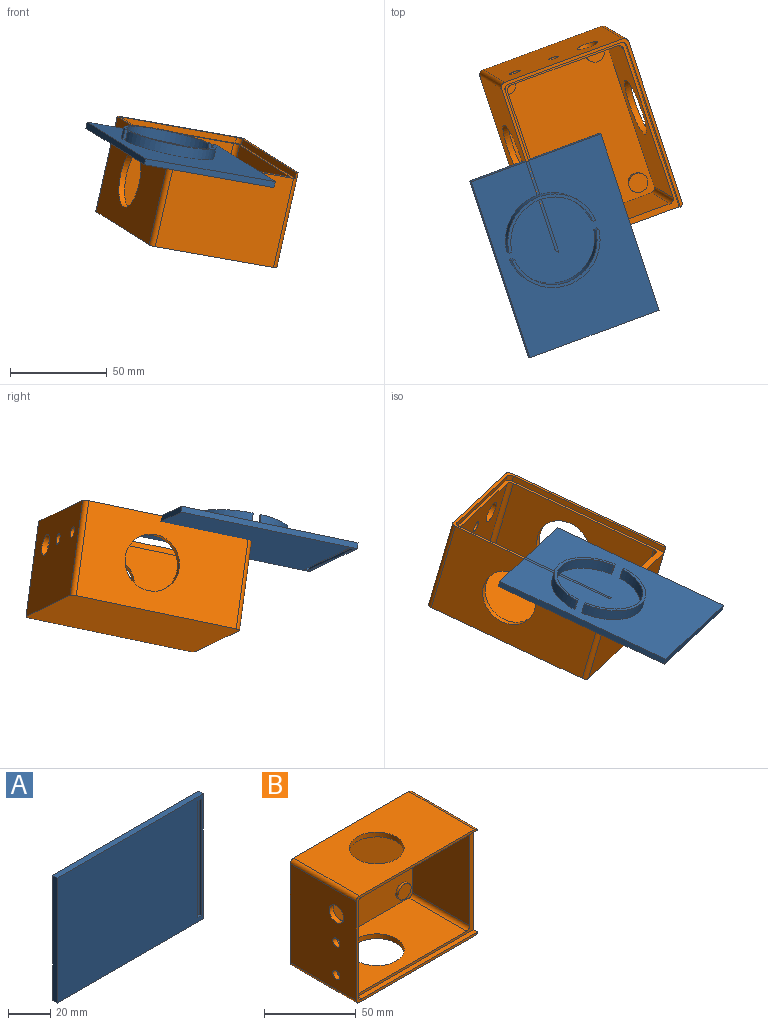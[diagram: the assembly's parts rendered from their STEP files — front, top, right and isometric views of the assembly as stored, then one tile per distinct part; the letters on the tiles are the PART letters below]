
ASSEMBLY  parts=2 mates=1
PART A: 21 faces, bbox 97.8x8.8x72.4 mm
  f0: cylinder r=22.86mm len=45.48mm, axis (0,-1,0), area 375.2mm2, adj f2,f8,f18,f20
  f1: cylinder r=24.45mm len=48.67mm, axis (0,-1,0), area 403.1mm2, adj f2,f8,f18,f20
  f2: plane 48.67x22.33mm, normal (0,1,0), area 110.6mm2, adj f0,f1,f18,f20
  f3: plane 97.79x72.39mm, normal (0,-1,0), area 6908.1mm2, adj f4,f5,f6,f7,f9,f10,f11,f12
  f4: plane 97.79x3.18mm, normal (0,0,1), area 310.5mm2, adj f3,f5,f7,f8
  f5: plane 72.39x3.18mm, normal (-1,0,0), area 229.8mm2, adj f3,f4,f6,f8
  f6: plane 97.79x3.18mm, normal (0,0,-1), area 310.5mm2, adj f3,f5,f7,f8
  f7: plane 72.39x3.18mm, normal (1,0,0), area 229.8mm2, adj f3,f4,f6,f8
  f8: plane 97.79x72.39mm, normal (0,1,0), area 6858mm2, adj f0,f1,f4,f5,f6,f7,f14,f15
  f9: plane 2.54x1.27mm, normal (0,0,-1), area 3.2mm2, adj f3,f10,f12,f13
  f10: plane 67.31x1.27mm, normal (1,0,0), area 85.5mm2, adj f3,f9,f11,f13
  f11: plane 2.54x1.27mm, normal (0,0,1), area 3.2mm2, adj f3,f10,f12,f13
  f12: plane 67.31x1.27mm, normal (-1,0,0), area 85.5mm2, adj f3,f9,f11,f13
  f13: plane 67.31x2.54mm, normal (0,-1,0), area 171mm2, adj f9,f10,f11,f12
  f14: cylinder r=22.86mm len=45.47mm, axis (0,-1,0), area 374.8mm2, adj f8,f16,f17,f19
  f15: cylinder r=24.45mm len=48.66mm, axis (0,-1,0), area 402.6mm2, adj f8,f16,f17,f19
  f16: plane 48.66x22.25mm, normal (0,1,0), area 110.4mm2, adj f14,f15,f17,f19
  f17: plane 5.59x1.59mm, normal (-1,0,0), area 8.9mm2, adj f8,f14,f15,f16
  f18: plane 5.59x1.59mm, normal (1,0,0), area 8.9mm2, adj f0,f1,f2,f8
  f19: plane 5.59x1.6mm, normal (-1,0,0), area 8.9mm2, adj f8,f14,f15,f16
  f20: plane 5.59x1.6mm, normal (1,0,0), area 8.9mm2, adj f0,f1,f2,f8
PART B: 38 faces, bbox 94x50.8x71.1 mm
  f0: plane 93.79x71.12mm, normal (0,-1,0), area 403.6mm2, adj f2,f3,f4,f5,f7,f8,f9,f10
  f1: plane 66.04x47.63mm, normal (1,0,0), area 3145.2mm2, adj f2,f6,f9,f13
  f2: cylinder r=2.54mm len=50.8mm, axis (0,1,0), area 199.6mm2, adj f0,f1,f3,f6,f10,f13
  f3: plane 88.9x50.8mm, normal (0,0,1), area 3809.3mm2, adj f0,f2,f6,f7,f33
  f4: plane 66.04x50.8mm, normal (-1,0,0), area 3207.7mm2, adj f0,f6,f7,f8,f35,f36,f37
  f5: plane 88.9x50.8mm, normal (0,0,-1), area 3809.3mm2, adj f0,f6,f8,f9,f34
  f6: plane 93.98x71.12mm, normal (0,1,0), area 6678.3mm2, adj f1,f2,f3,f4,f5,f7,f8,f9
  f7: cylinder r=2.54mm len=50.8mm, axis (0,-1,0), area 202.7mm2, adj f0,f3,f4,f6
  f8: cylinder r=2.54mm len=50.8mm, axis (0,1,0), area 202.7mm2, adj f0,f4,f5,f6
  f9: cylinder r=2.54mm len=50.8mm, axis (0,-1,0), area 199.6mm2, adj f0,f1,f5,f6,f12,f13
  f10: plane 89.67x3.18mm, normal (0,0,-1), area 284.7mm2, adj f0,f2,f13,f23
  f11: plane 62.87x3.18mm, normal (1,0,0), area 199.6mm2, adj f0,f13,f23,f24
  f12: plane 89.67x3.18mm, normal (0,0,1), area 284.7mm2, adj f0,f9,f13,f24
  f13: plane 92.39x67.95mm, normal (0,-1,0), area 604.5mm2, adj f1,f2,f9,f10,f11,f12,f15,f16
  f14: plane 87.63x64.77mm, normal (0,-1,0), area 5346mm2, adj f15,f16,f17,f18,f19,f20,f21,f22
  f15: cylinder r=2.54mm len=44.32mm, axis (0,-1,0), area 176.8mm2, adj f13,f14,f21,f22
  f16: cylinder r=2.54mm len=44.32mm, axis (0,1,0), area 176.8mm2, adj f13,f14,f20,f21
  f17: cylinder r=2.54mm len=44.32mm, axis (0,1,0), area 176.8mm2, adj f13,f14,f19,f22
  f18: cylinder r=2.54mm len=44.32mm, axis (0,-1,0), area 176.8mm2, adj f13,f14,f19,f20
  f19: plane 59.69x44.32mm, normal (-1,0,0), area 2645.6mm2, adj f13,f14,f17,f18
  f20: plane 82.55x44.32mm, normal (0,0,1), area 2952mm2, adj f13,f14,f16,f18,f34
  f21: plane 59.69x44.32mm, normal (1,0,0), area 2498.5mm2, adj f13,f14,f15,f16,f35,f36,f37
  f22: plane 82.55x44.32mm, normal (0,0,-1), area 2952mm2, adj f13,f14,f15,f17,f33
  f23: cylinder r=2.54mm len=3.18mm, axis (0,-1,0), area 12.7mm2, adj f0,f10,f11,f13
  f24: cylinder r=2.54mm len=3.18mm, axis (0,1,0), area 12.7mm2, adj f0,f11,f12,f13
  f25: cylinder r=5.08mm len=10.16mm, axis (0,1,0), area 52.7mm2, adj f14,f26
  f26: plane 10.16x10.16mm, normal (0,-1,0), area 81.1mm2, adj f25
  f27: cylinder r=5.08mm len=10.16mm, axis (0,1,0), area 52.7mm2, adj f14,f28
  f28: plane 10.16x10.16mm, normal (0,-1,0), area 81.1mm2, adj f27
  f29: cylinder r=5.08mm len=10.16mm, axis (0,1,0), area 52.7mm2, adj f14,f30
  f30: plane 10.16x10.16mm, normal (0,-1,0), area 81.1mm2, adj f29
  f31: cylinder r=5.08mm len=10.16mm, axis (0,1,0), area 52.7mm2, adj f14,f32
  f32: plane 10.16x10.16mm, normal (0,-1,0), area 81.1mm2, adj f31
  f33: cylinder r=15mm len=30mm, axis (0,0,-1), area 299.2mm2, adj f3,f22
  f34: cylinder r=15mm len=30mm, axis (0,0,-1), area 299.2mm2, adj f5,f20
  f35: cylinder r=5.59mm len=11.18mm, axis (-1,0,0), area 111.5mm2, adj f4,f21
  f36: cylinder r=2.79mm len=5.59mm, axis (-1,0,0), area 55.7mm2, adj f4,f21
  f37: cylinder r=2.79mm len=5.59mm, axis (-1,0,0), area 55.7mm2, adj f4,f21
PLACE A rot(axis=(0.69,-0.39,-0.61),109.1deg) t=(133.18,-71.45,28.43)mm
PLACE B rot(axis=(-0.7,0.6,-0.38),111.2deg) t=(68.79,-35.62,-4.8)mm
MATE slider B.f13 <-> A.f3  axis (0.22,-0.13,0.97) through (83.48,-36.84,40.95)mm
